# Revit family: ВКДВ
name_source: partatom
category: Оборудование
units: mm (PartAtom-declared; Revit-internal decimal feet)

## family parameters
Всегда вертикально = Да
Классификация = Нет
На основе рабочей плоскости = Нет
Общий = Нет
При загрузке вырезать с полостями = Нет
Размер круглого соединителя = Использовать диаметр
Тип детали = Нормальный
Точка принадлежности помещению = Нет

## types (38) — shared parameters
00_20_Manufacturer = Вентс
00_20_Name = Вентилятор даховий димовидалення
Grid Material = Cover Grid Cross
Load Classification = HVAC
Maintenance zone material = <По категории>
Maximum Air Flow = 0.0 л/с
Number of Fase = 3
Voltage = 400 В
h2 = 248 мм
zero-valued in all types: Отметка по умолчанию

## per-type parameters (varying)
- ВКДВ 630-600-1,5/930: Casing Material=<По категории>; D1=541 мм; D2=634 мм; Dn=513 мм; Dy=503 мм; H=1038 мм; H1=302 мм; H3=519 мм; H4=411 мм; L1=1424 мм; L3=955 мм; Power=1500 В·А; R1=271 мм; R2=317 мм; Rn=257 мм; Ry=252 мм; d1=10 мм; h1=151 мм; h4=779 мм; l3=382 мм; l33=805 мм; l333=478 мм; l4=310 мм; n=12; Вес=200 кг
- ВКДВ 1100-600-37/980: Casing Material=<По категории>; D1=934 мм; D2=1075 мм; Dn=913 мм; Dy=903 мм; H=1773 мм; H1=441 мм; H3=887 мм; H4=664 мм; L1=2236 мм; L3=1430 мм; Power=37000 В·А; R1=467 мм; R2=538 мм; Rn=457 мм; Ry=452 мм; d1=12 мм; h1=221 мм; h4=1330 мм; l3=572 мм; l33=1280 мм; l333=715 мм; l4=474 мм; n=24; Вес=930 кг
- ВКДВ 630-600-2,2/940: Casing Material=Металл, окрашенный, синий, матовый RAL 5007; D1=541 мм; D2=634 мм; Dn=513 мм; Dy=503 мм; H=1038 мм; H1=426 мм; H3=519 мм; H4=473 мм; L1=1424 мм; L3=955 мм; Power=2200 В·А; R1=271 мм; R2=317 мм; Rn=257 мм; Ry=252 мм; d1=10 мм; h1=213 мм; h4=779 мм; l3=382 мм; l33=805 мм; l333=478 мм; l4=310 мм; n=12; Вес=210 кг
- ВКДВ 630-600-3/960: Casing Material=<По категории>; D1=541 мм; D2=634 мм; Dn=513 мм; Dy=503 мм; H=1043 мм; H1=307 мм; H3=522 мм; H4=414 мм; L1=1424 мм; L3=955 мм; Power=3000 В·А; R1=271 мм; R2=317 мм; Rn=257 мм; Ry=252 мм; d1=10 мм; h1=154 мм; h4=782 мм; l3=382 мм; l33=805 мм; l333=478 мм; l4=310 мм; n=12; Вес=225 кг
- ВКДВ 630-600-4/1440: Casing Material=<По категории>; D1=541 мм; D2=634 мм; Dn=513 мм; Dy=503 мм; H=1038 мм; H1=302 мм; H3=519 мм; H4=411 мм; L1=1424 мм; L3=955 мм; Power=4000 В·А; R1=271 мм; R2=317 мм; Rn=257 мм; Ry=252 мм; d1=10 мм; h1=151 мм; h4=779 мм; l3=382 мм; l33=805 мм; l333=478 мм; l4=310 мм; n=12; Вес=216 кг
- ВКДВ 630-600-5,5/1450: Casing Material=<По категории>; D1=541 мм; D2=634 мм; Dn=513 мм; Dy=503 мм; H=1043 мм; H1=307 мм; H3=522 мм; H4=414 мм; L1=1424 мм; L3=955 мм; Power=5500 В·А; R1=271 мм; R2=317 мм; Rn=257 мм; Ry=252 мм; d1=10 мм; h1=154 мм; h4=782 мм; l3=382 мм; l33=805 мм; l333=478 мм; l4=310 мм; n=12; Вес=230 кг
- ВКДВ 630-600-7,5/1440: Casing Material=<По категории>; D1=541 мм; D2=634 мм; Dn=513 мм; Dy=503 мм; H=1134 мм; H1=307 мм; H3=567 мм; H4=437 мм; L1=1424 мм; L3=955 мм; Power=7500 В·А; R1=271 мм; R2=317 мм; Rn=257 мм; Ry=252 мм; d1=10 мм; h1=154 мм; h4=851 мм; l3=382 мм; l33=805 мм; l333=478 мм; l4=310 мм; n=12; Вес=255 кг
- ВКДВ 710-600-2,2/940: Casing Material=<По категории>; D1=674 мм; D2=730 мм; Dn=643 мм; Dy=633 мм; H=1181 мм; H1=317 мм; H3=591 мм; H4=454 мм; L1=1508 мм; L3=1040 мм; Power=2200 В·А; R1=337 мм; R2=365 мм; Rn=322 мм; Ry=317 мм; d1=12 мм; h1=159 мм; h4=886 мм; l3=416 мм; l33=890 мм; l333=520 мм; l4=339 мм; n=16; Вес=242 кг
- ВКДВ 710-600-3/960: Casing Material=<По категории>; D1=674 мм; D2=730 мм; Dn=643 мм; Dy=633 мм; H=1186 мм; H1=322 мм; H3=593 мм; H4=458 мм; L1=1508 мм; L3=1040 мм; Power=3000 В·А; R1=337 мм; R2=365 мм; Rn=322 мм; Ry=317 мм; d1=12 мм; h1=161 мм; h4=890 мм; l3=416 мм; l33=890 мм; l333=520 мм; l4=339 мм; n=16; Вес=252 кг
- ВКДВ 710-600-4/950: Casing Material=<По категории>; D1=674 мм; D2=730 мм; Dn=643 мм; Dy=633 мм; H=1186 мм; H1=322 мм; H3=593 мм; H4=458 мм; L1=1508 мм; L3=1040 мм; Power=4000 В·А; R1=337 мм; R2=365 мм; Rn=322 мм; Ry=317 мм; d1=12 мм; h1=161 мм; h4=890 мм; l3=416 мм; l33=890 мм; l333=520 мм; l4=339 мм; n=16; Вес=253 кг
- ВКДВ 710-600-5,5/960: Casing Material=<По категории>; D1=674 мм; D2=730 мм; Dn=643 мм; Dy=633 мм; H=1186 мм; H1=322 мм; H3=593 мм; H4=458 мм; L1=1508 мм; L3=1040 мм; Power=5500 В·А; R1=337 мм; R2=365 мм; Rn=322 мм; Ry=317 мм; d1=12 мм; h1=161 мм; h4=890 мм; l3=416 мм; l33=890 мм; l333=520 мм; l4=339 мм; n=16; Вес=280 кг
- ВКДВ 710-600-7,5/1455: Casing Material=<По категории>; D1=674 мм; D2=730 мм; Dn=643 мм; Dy=633 мм; H=1186 мм; H1=322 мм; H3=593 мм; H4=458 мм; L1=1508 мм; L3=1040 мм; Power=7500 В·А; R1=337 мм; R2=365 мм; Rn=322 мм; Ry=317 мм; d1=12 мм; h1=161 мм; h4=890 мм; l3=416 мм; l33=890 мм; l333=520 мм; l4=339 мм; n=16; Вес=281 кг
- ВКДВ 710-600-11/1460: Casing Material=<По категории>; D1=674 мм; D2=730 мм; Dn=643 мм; Dy=633 мм; H=1186 мм; H1=322 мм; H3=593 мм; H4=458 мм; L1=1508 мм; L3=1040 мм; Power=11000 В·А; R1=337 мм; R2=365 мм; Rn=322 мм; Ry=317 мм; d1=12 мм; h1=161 мм; h4=890 мм; l3=416 мм; l33=890 мм; l333=520 мм; l4=339 мм; n=16; Вес=292 кг
- ВКДВ 800-600-4/960: Casing Material=<По категории>; D1=674 мм; D2=784 мм; Dn=643 мм; Dy=633 мм; H=1239 мм; H1=345 мм; H3=620 мм; H4=482 мм; L1=1543 мм; L3=1040 мм; Power=4000 В·А; R1=337 мм; R2=392 мм; Rn=322 мм; Ry=317 мм; d1=12 мм; h1=173 мм; h4=929 мм; l3=416 мм; l33=890 мм; l333=520 мм; l4=339 мм; n=16; Вес=286 кг
- ВКДВ 800-600-5,5/950: Casing Material=<По категории>; D1=674 мм; D2=784 мм; Dn=643 мм; Dy=633 мм; H=1239 мм; H1=345 мм; H3=620 мм; H4=482 мм; L1=1543 мм; L3=1040 мм; Power=5500 В·А; R1=337 мм; R2=392 мм; Rn=322 мм; Ry=317 мм; d1=12 мм; h1=173 мм; h4=929 мм; l3=416 мм; l33=890 мм; l333=520 мм; l4=339 мм; n=16; Вес=305 кг
- ВКДВ 800-600-7,5/970: Casing Material=<По категории>; D1=674 мм; D2=784 мм; Dn=643 мм; Dy=633 мм; H=1239 мм; H1=345 мм; H3=620 мм; H4=482 мм; L1=1543 мм; L3=1040 мм; Power=7500 В·А; R1=337 мм; R2=392 мм; Rn=322 мм; Ry=317 мм; d1=12 мм; h1=173 мм; h4=929 мм; l3=416 мм; l33=890 мм; l333=520 мм; l4=339 мм; n=16; Вес=312 кг
- ВКДВ 800-600-11/960: Casing Material=<По категории>; D1=674 мм; D2=784 мм; Dn=643 мм; Dy=633 мм; H=1335 мм; H1=355 мм; H3=668 мм; H4=511 мм; L1=1543 мм; L3=1040 мм; Power=11000 В·А; R1=337 мм; R2=392 мм; Rn=322 мм; Ry=317 мм; d1=12 мм; h1=178 мм; h4=1001 мм; l3=416 мм; l33=890 мм; l333=520 мм; l4=338 мм; n=16; Вес=390 кг
- ВКДВ 800-600-15/1460: Casing Material=<По категории>; D1=674 мм; D2=784 мм; Dn=643 мм; Dy=633 мм; H=1335 мм; H1=355 мм; H3=668 мм; H4=511 мм; L1=1543 мм; L3=1040 мм; Power=15000 В·А; R1=337 мм; R2=392 мм; Rn=322 мм; Ry=317 мм; d1=12 мм; h1=178 мм; h4=1001 мм; l3=416 мм; l33=890 мм; l333=520 мм; l4=338 мм; n=16; Вес=390 кг
- ВКДВ 800-600-18,5/1470: Casing Material=<По категории>; D1=674 мм; D2=784 мм; Dn=643 мм; Dy=633 мм; H=1335 мм; H1=355 мм; H3=668 мм; H4=511 мм; L1=1543 мм; L3=1040 мм; Power=18500 В·А; R1=337 мм; R2=392 мм; Rn=322 мм; Ry=317 мм; d1=12 мм; h1=178 мм; h4=1001 мм; l3=416 мм; l33=890 мм; l333=520 мм; l4=338 мм; n=16; Вес=395 кг
- ВКДВ 900-600-4/720: Casing Material=<По категории>; D1=751 мм; D2=874 мм; Dn=723 мм; Dy=713 мм; H=1379 мм; H1=363 мм; H3=690 мм; H4=526 мм; L1=1871 мм; L3=1200 мм; Power=4000 В·А; R1=376 мм; R2=437 мм; Rn=362 мм; Ry=357 мм; d1=12 мм; h1=182 мм; h4=1034 мм; l3=480 мм; l33=1050 мм; l333=600 мм; l4=394 мм; n=16; Вес=376 кг
- ВКДВ 900-600-5,5/960: Casing Material=<По категории>; D1=751 мм; D2=874 мм; Dn=723 мм; Dy=713 мм; H=1398 мм; H1=363 мм; H3=699 мм; H4=531 мм; L1=1871 мм; L3=1200 мм; Power=5500 В·А; R1=376 мм; R2=437 мм; Rn=362 мм; Ry=357 мм; d1=12 мм; h1=182 мм; h4=1049 мм; l3=480 мм; l33=1050 мм; l333=600 мм; l4=394 мм; n=16; Вес=376 кг
- ВКДВ 900-600-7,5/970: Casing Material=<По категории>; D1=751 мм; D2=874 мм; Dn=723 мм; Dy=713 мм; H=1398 мм; H1=363 мм; H3=699 мм; H4=531 мм; L1=1871 мм; L3=1200 мм; Power=7500 В·А; R1=376 мм; R2=437 мм; Rn=362 мм; Ry=357 мм; d1=12 мм; h1=182 мм; h4=1049 мм; l3=480 мм; l33=1050 мм; l333=600 мм; l4=394 мм; n=16; Вес=380 кг
- ВКДВ 900-600-11/970: Casing Material=<По категории>; D1=751 мм; D2=874 мм; Dn=723 мм; Dy=713 мм; H=1398 мм; H1=372 мм; H3=699 мм; H4=536 мм; L1=1871 мм; L3=1200 мм; Power=11000 В·А; R1=376 мм; R2=437 мм; Rn=362 мм; Ry=357 мм; d1=12 мм; h1=186 мм; h4=1049 мм; l3=480 мм; l33=1050 мм; l333=600 мм; l4=394 мм; n=16; Вес=418 кг
- ВКДВ 900-600-15/960: Casing Material=<По категории>; D1=751 мм; D2=874 мм; Dn=723 мм; Dy=713 мм; H=1398 мм; H1=372 мм; H3=699 мм; H4=536 мм; L1=1871 мм; L3=1200 мм; Power=15000 В·А; R1=376 мм; R2=437 мм; Rn=362 мм; Ry=357 мм; d1=12 мм; h1=186 мм; h4=1049 мм; l3=480 мм; l33=1050 мм; l333=600 мм; l4=394 мм; n=16; Вес=433 кг
- ВКДВ 900-600-18,5/960: Casing Material=<По категории>; D1=751 мм; D2=874 мм; Dn=723 мм; Dy=713 мм; H=1491 мм; H1=372 мм; H3=746 мм; H4=559 мм; L1=1871 мм; L3=1200 мм; Power=18500 В·А; R1=376 мм; R2=437 мм; Rn=362 мм; Ry=357 мм; d1=12 мм; h1=186 мм; h4=1118 мм; l3=480 мм; l33=1050 мм; l333=600 мм; l4=394 мм; n=16; Вес=482 кг
- ВКДВ 900-600-22/960: Casing Material=<По категории>; D1=751 мм; D2=874 мм; Dn=723 мм; Dy=713 мм; H=1565 мм; H1=372 мм; H3=783 мм; H4=577 мм; L1=1871 мм; L3=1200 мм; Power=22000 В·А; R1=376 мм; R2=437 мм; Rn=362 мм; Ry=357 мм; d1=12 мм; h1=186 мм; h4=1174 мм; l3=480 мм; l33=1050 мм; l333=600 мм; l4=394 мм; n=16; Вес=566 кг
- ВКДВ 1000-600-5,5/720: Casing Material=<По категории>; D1=837 мм; D2=974 мм; Dn=813 мм; Dy=803 мм; H=1365 мм; H1=398 мм; H3=683 мм; H4=540 мм; L1=2111 мм; L3=1430 мм; Power=5500 В·А; R1=419 мм; R2=487 мм; Rn=407 мм; Ry=402 мм; d1=12 мм; h1=199 мм; h4=1024 мм; l3=572 мм; l33=1280 мм; l333=715 мм; l4=473 мм; n=24; Вес=467 кг
- ВКДВ 1000-600-7,5/730: Casing Material=<По категории>; D1=837 мм; D2=974 мм; Dn=813 мм; Dy=803 мм; H=1573 мм; H1=403 мм; H3=787 мм; H4=595 мм; L1=2111 мм; L3=1430 мм; Power=7500 В·А; R1=419 мм; R2=487 мм; Rn=407 мм; Ry=402 мм; d1=12 мм; h1=202 мм; h4=1180 мм; l3=572 мм; l33=1280 мм; l333=715 мм; l4=476 мм; n=24; Вес=588 кг
- ВКДВ 1000-600-11/970: Casing Material=<По категории>; D1=837 мм; D2=974 мм; Dn=813 мм; Dy=803 мм; H=1573 мм; H1=403 мм; H3=787 мм; H4=595 мм; L1=2111 мм; L3=1430 мм; Power=11000 В·А; R1=419 мм; R2=487 мм; Rn=407 мм; Ry=402 мм; d1=12 мм; h1=202 мм; h4=1180 мм; l3=572 мм; l33=1280 мм; l333=715 мм; l4=476 мм; n=24; Вес=590 кг
- ВКДВ 1000-600-15/970: Casing Material=<По категории>; D1=837 мм; D2=974 мм; Dn=813 мм; Dy=803 мм; H=1573 мм; H1=403 мм; H3=787 мм; H4=595 мм; L1=2111 мм; L3=1430 мм; Power=15000 В·А; R1=419 мм; R2=487 мм; Rn=407 мм; Ry=402 мм; d1=12 мм; h1=202 мм; h4=1180 мм; l3=572 мм; l33=1280 мм; l333=715 мм; l4=476 мм; n=24; Вес=595 кг
- ВКДВ 1000-600-18,5/970: Casing Material=<По категории>; D1=837 мм; D2=974 мм; Dn=813 мм; Dy=803 мм; H=1573 мм; H1=403 мм; H3=787 мм; H4=595 мм; L1=2111 мм; L3=1430 мм; Power=18500 В·А; R1=419 мм; R2=487 мм; Rn=407 мм; Ry=402 мм; d1=12 мм; h1=202 мм; h4=1180 мм; l3=572 мм; l33=1280 мм; l333=715 мм; l4=476 мм; n=24; Вес=639 кг
- ВКДВ 1000-600-22/970: Casing Material=<По категории>; D1=837 мм; D2=974 мм; Dn=813 мм; Dy=803 мм; H=1573 мм; H1=403 мм; H3=787 мм; H4=595 мм; L1=2111 мм; L3=1430 мм; Power=22000 В·А; R1=419 мм; R2=487 мм; Rn=407 мм; Ry=402 мм; d1=12 мм; h1=202 мм; h4=1180 мм; l3=572 мм; l33=1280 мм; l333=715 мм; l4=476 мм; n=24; Вес=670 кг
- ВКДВ 1000-600-30/970: Casing Material=<По категории>; D1=837 мм; D2=974 мм; Dn=813 мм; Dy=803 мм; H=1573 мм; H1=403 мм; H3=787 мм; H4=595 мм; L1=2111 мм; L3=1430 мм; Power=30000 В·А; R1=419 мм; R2=487 мм; Rn=407 мм; Ry=402 мм; d1=12 мм; h1=202 мм; h4=1180 мм; l3=572 мм; l33=1280 мм; l333=715 мм; l4=476 мм; n=24; Вес=690 кг
- ВКДВ 1100-600-11/730: Casing Material=<По категории>; D1=934 мм; D2=1075 мм; Dn=913 мм; Dy=903 мм; H=1721 мм; H1=441 мм; H3=861 мм; H4=651 мм; L1=2236 мм; L3=1430 мм; Power=11000 В·А; R1=467 мм; R2=538 мм; Rn=457 мм; Ry=452 мм; d1=12 мм; h1=221 мм; h4=1291 мм; l3=572 мм; l33=1280 мм; l333=715 мм; l4=474 мм; n=24; Вес=720 кг
- ВКДВ 1100-600-15/730: Casing Material=<По категории>; D1=934 мм; D2=1075 мм; Dn=913 мм; Dy=903 мм; H=1721 мм; H1=441 мм; H3=861 мм; H4=651 мм; L1=2236 мм; L3=1430 мм; Power=15000 В·А; R1=467 мм; R2=538 мм; Rn=457 мм; Ry=452 мм; d1=12 мм; h1=221 мм; h4=1291 мм; l3=572 мм; l33=1280 мм; l333=715 мм; l4=474 мм; n=24; Вес=775 кг
- ВКДВ 1100-600-18,5/970: Casing Material=<По категории>; D1=934 мм; D2=1075 мм; Dn=913 мм; Dy=903 мм; H=1721 мм; H1=441 мм; H3=861 мм; H4=651 мм; L1=2236 мм; L3=1430 мм; Power=18500 В·А; R1=467 мм; R2=538 мм; Rn=457 мм; Ry=452 мм; d1=12 мм; h1=221 мм; h4=1291 мм; l3=572 мм; l33=1280 мм; l333=715 мм; l4=474 мм; n=24; Вес=763 кг
- ВКДВ 1100-600-22/970: Casing Material=<По категории>; D1=934 мм; D2=1075 мм; Dn=913 мм; Dy=903 мм; H=1721 мм; H1=441 мм; H3=861 мм; H4=651 мм; L1=2236 мм; L3=1430 мм; Power=22000 В·А; R1=467 мм; R2=538 мм; Rn=457 мм; Ry=452 мм; d1=12 мм; h1=221 мм; h4=1291 мм; l3=572 мм; l33=1280 мм; l333=715 мм; l4=474 мм; n=24; Вес=794 кг
- ВКДВ 1100-600-30/970: Casing Material=<По категории>; D1=934 мм; D2=1075 мм; Dn=913 мм; Dy=903 мм; H=1721 мм; H1=441 мм; H3=861 мм; H4=651 мм; L1=2236 мм; L3=1430 мм; Power=30000 В·А; R1=467 мм; R2=538 мм; Rn=457 мм; Ry=452 мм; d1=12 мм; h1=221 мм; h4=1291 мм; l3=572 мм; l33=1280 мм; l333=715 мм; l4=474 мм; n=24; Вес=812 кг

note: column(s) folded — value = type name in every type: 00_20_Type
